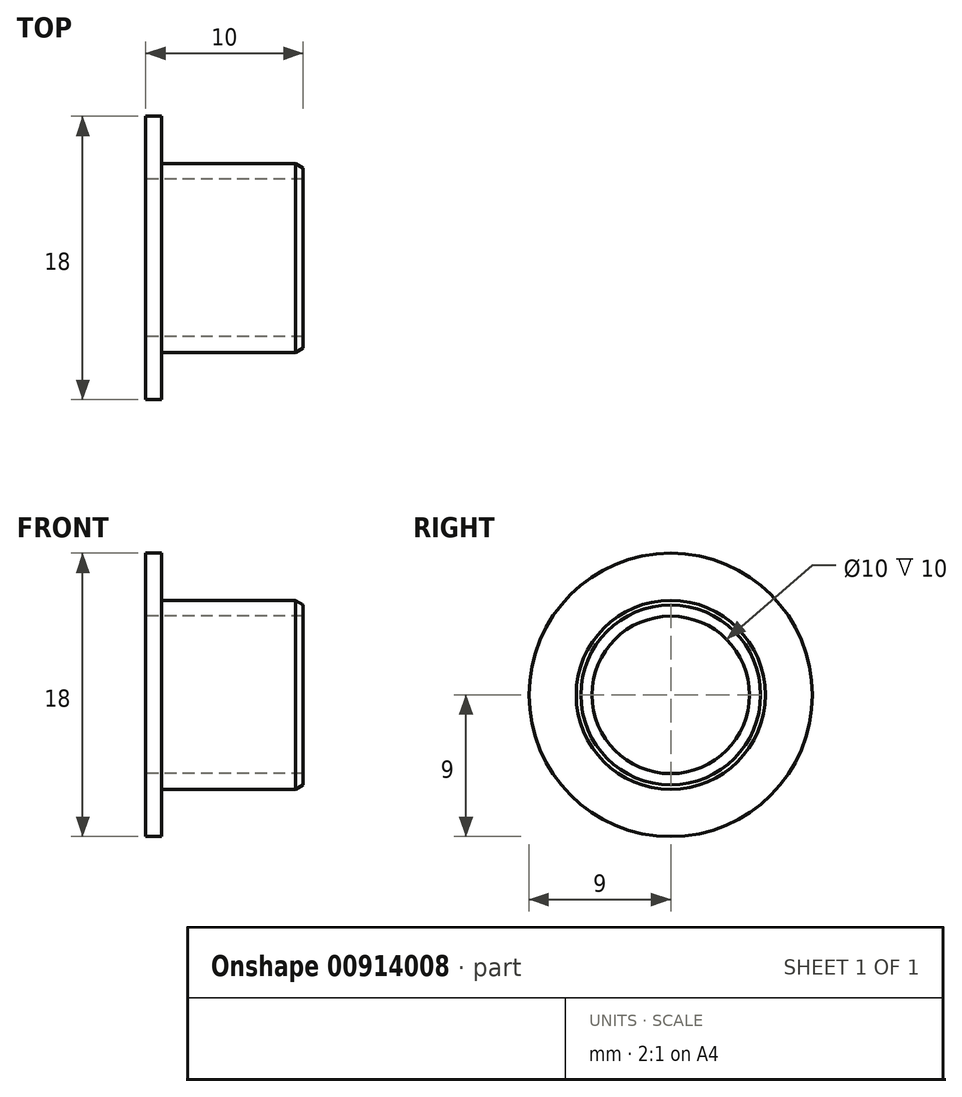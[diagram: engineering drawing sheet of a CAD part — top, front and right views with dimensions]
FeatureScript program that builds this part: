
annotation { "Feature Type Name" : "Feature", "Feature Type Description" : "" }
export const myFeature = defineFeature(function(context is Context, id is Id, definition is map)
    precondition{}
    {
        {
            var Q0;
            Q0=qCreatedBy(makeId("Front.planeOp"),FACE);
            var sketch = newSketch(context, id + "F0", { "sketchPlane" : qUnion([Q0])});
            skLineSegment(sketch, "E0", {"start": v(-14.71, 0) * mm, "end": v(17.2, 0) * mm, "construction": true});
            skLineSegment(sketch, "E1", {"start": v(-1, 9) * mm, "end": v(-1, 5) * mm});
            skLineSegment(sketch, "E2", {"start": v(-1, 5) * mm, "end": v(9, 5) * mm});
            skLineSegment(sketch, "E3", {"start": v(-1, 9) * mm, "end": v(0, 9) * mm});
            skLineSegment(sketch, "E4", {"start": v(0, 9) * mm, "end": v(0, 6) * mm});
            skLineSegment(sketch, "E5", {"start": v(0, 6) * mm, "end": v(8.5, 6) * mm});
            skLineSegment(sketch, "E6", {"start": v(8.5, 6) * mm, "end": v(9, 5.71) * mm});
            skLineSegment(sketch, "E7", {"start": v(9, 5.71) * mm, "end": v(9, 5) * mm});
            skSolve(sketch);
        }
        {
            var Q0;
            Q0 = qSketchRegion(id + "F0", true);
            var Q1;
            Q1=sQuery(id+"F0.wireOp",EDGE,"E0");
            revolve(context, id + "F1", {"surfaceOperationType" : NewSurfaceOperationType.NEW, "entities" : qUnion([Q0]), "axis" : qUnion([Q1]), "revolveType" : RevolveType.FULL});
        }
    });
